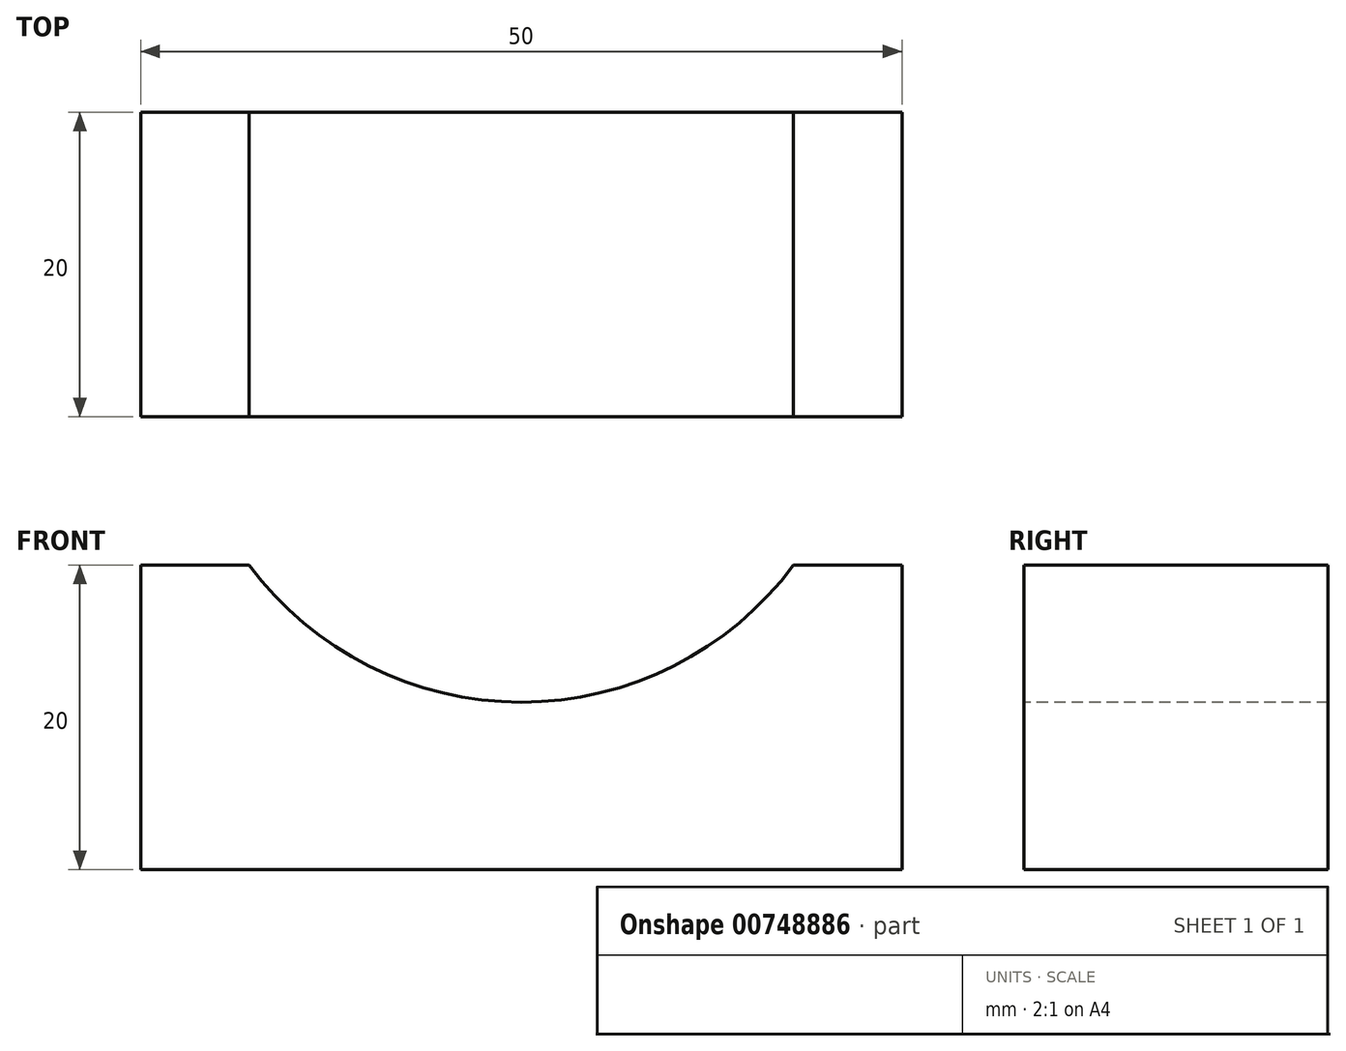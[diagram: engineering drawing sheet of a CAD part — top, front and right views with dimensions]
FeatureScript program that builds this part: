
annotation { "Feature Type Name" : "Feature", "Feature Type Description" : "" }
export const myFeature = defineFeature(function(context is Context, id is Id, definition is map)
    precondition{}
    {
        {
            var Q0;
            Q0=qCreatedBy(makeId("Top.planeOp"),FACE);
            var sketch = newSketch(context, id + "F0", { "sketchPlane" : qUnion([Q0])});
            skLineSegment(sketch, "E0.bottom", {"start": v(-25, -10) * mm, "end": v(25, -10) * mm});
            skLineSegment(sketch, "E0.top", {"start": v(-25, 10) * mm, "end": v(25, 10) * mm});
            skLineSegment(sketch, "E0.left", {"start": v(-25, -10) * mm, "end": v(-25, 10) * mm});
            skLineSegment(sketch, "E0.right", {"start": v(25, -10) * mm, "end": v(25, 10) * mm});
            skPoint(sketch, "E0.middle", {"position": v(0, 0) * mm});
            skSolve(sketch);
        }
        {
            var Q0;
            Q0=qSketchRegion(id+"F0",true);
            extrude(context, id + "F1", {"entities" : qUnion([Q0]), "depth" : 20 * mm, "offsetDistance" : 25 * mm});
        }
        {
            var Q0;
            Q0=makeQuery(id+"F1.opExtrude","SWEPT_FACE",FACE,{"disambiguationData":[OSD([sQuery(id+"F0.wireOp",EDGE,"E0.bottom")])]});
            var sketch = newSketch(context, id + "F2", { "sketchPlane" : qUnion([Q0])});
            skCircle(sketch, "E1", {"center": v(0, 33.25) * mm, "radius": 22.25 * mm});
            skSolve(sketch);
        }
        {
            var Q0;
            Q0=qSketchRegion(id+"F2",true);
            extrude(context, id + "F3", {"entities" : qUnion([Q0]), "operationType" : NewBodyOperationType.REMOVE, "oppositeDirection" : true, "depth" : 25 * mm, "offsetDistance" : 25 * mm});
        }
    });
